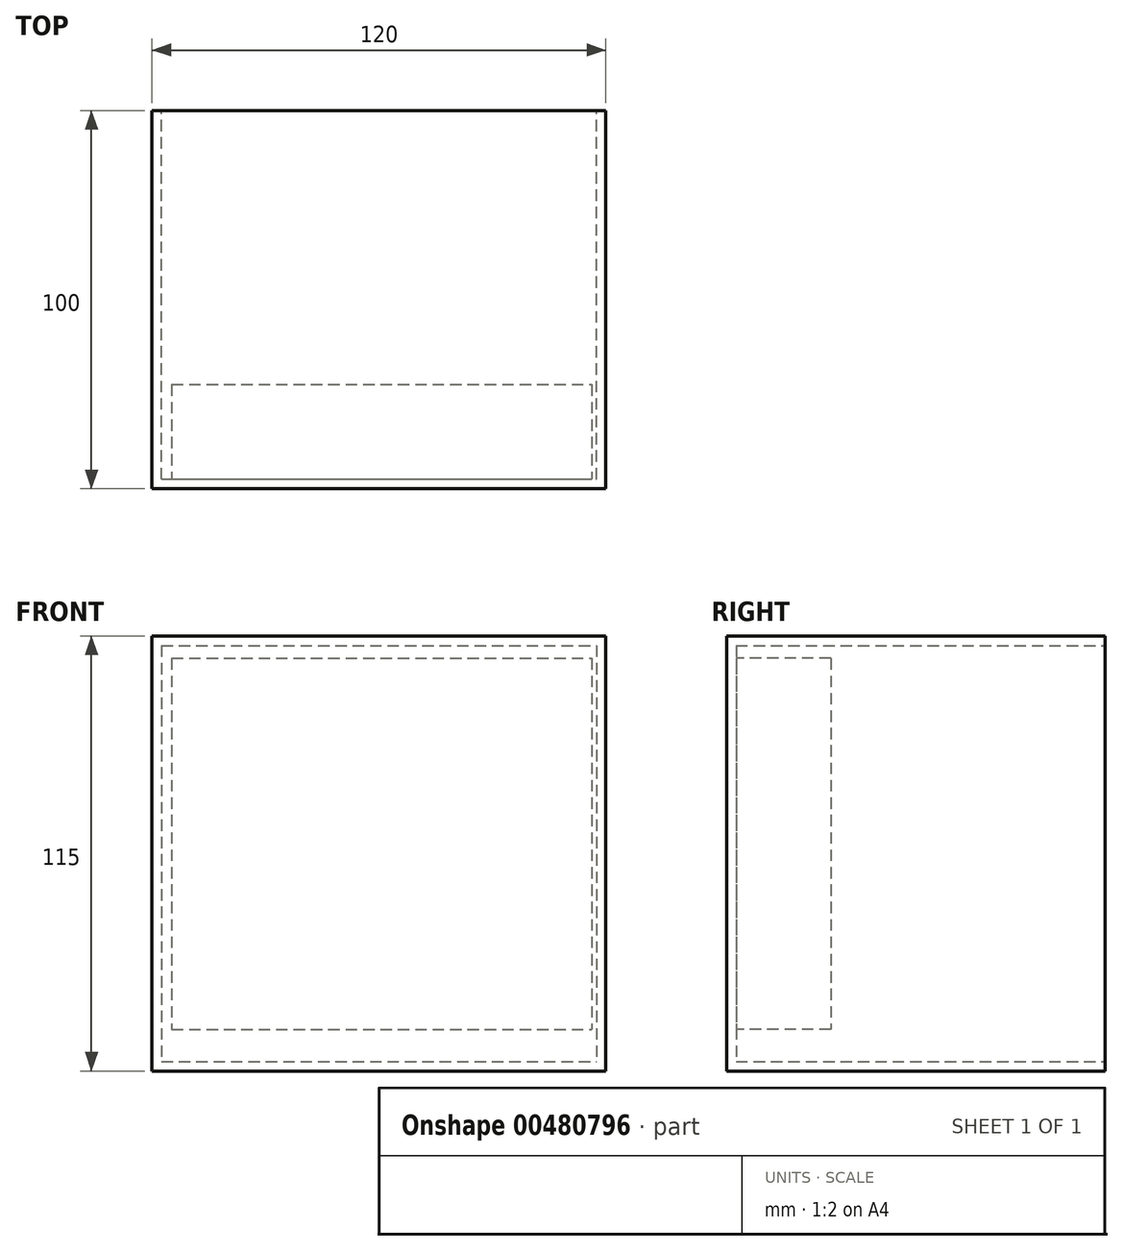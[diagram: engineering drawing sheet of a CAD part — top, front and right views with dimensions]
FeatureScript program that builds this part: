
annotation { "Feature Type Name" : "Feature", "Feature Type Description" : "" }
export const myFeature = defineFeature(function(context is Context, id is Id, definition is map)
    precondition{}
    {
        {
            var Q0;
            Q0=qCreatedBy(makeId("Front.planeOp"),FACE);
            var sketch = newSketch(context, id + "F0", { "sketchPlane" : qUnion([Q0])});
            skLineSegment(sketch, "E0.bottom", {"start": v(40, 25) * mm, "end": v(-40, 25) * mm});
            skLineSegment(sketch, "E0.top", {"start": v(40, -25) * mm, "end": v(-40, -25) * mm});
            skLineSegment(sketch, "E0.left", {"start": v(40, 25) * mm, "end": v(40, -25) * mm});
            skLineSegment(sketch, "E0.right", {"start": v(-40, 25) * mm, "end": v(-40, -25) * mm});
            skPoint(sketch, "E0.middle", {"position": v(0, 0) * mm});
            skLineSegment(sketch, "E1.bottom", {"start": v(-38.55, 20) * mm, "end": v(31.45, 20) * mm});
            skLineSegment(sketch, "E1.top", {"start": v(-38.55, -20) * mm, "end": v(31.45, -20) * mm});
            skLineSegment(sketch, "E1.left", {"start": v(-38.55, 20) * mm, "end": v(-38.55, -20) * mm});
            skLineSegment(sketch, "E1.right", {"start": v(31.45, 20) * mm, "end": v(31.45, -20) * mm});
            skPoint(sketch, "E1.middle", {"position": v(-3.55, 0) * mm});
            skSolve(sketch);
        }
        {
            var Q0;
            Q0=makeQuery(id+"F0.imprint","IMPRINT",FACE,{"disambiguationData":[TD([[makeQuery(id+"F0.imprint","IMPRINT",EDGE,{"derivedFrom":sQuery(id+"F0.wireOp",EDGE,"E1.bottom")}),-1.0]])]});
            extrude(context, id + "F1", {"entities" : qUnion([Q0]), "depth" : 25 * mm});
        }
        {
            var Q0;
            Q0=makeQuery(id+"F1.opExtrude","SWEPT_FACE",FACE,{"disambiguationData":[OSD([sQuery(id+"F0.wireOp",EDGE,"E1.left")])]});
            extrude(context, id + "F2", {"entities" : qUnion([Q0]), "operationType" : NewBodyOperationType.ADD, "depth" : 25 * mm});
        }
        {
            var Q0;
            Q0=makeQuery(id+"F2.opExtrude","CAP_FACE",FACE,{"disambiguationData":[OSD([sQuery(id+"F0.wireOp",EDGE,"E1.left")])],"isStart":false});
            extrude(context, id + "F3", {"entities" : qUnion([Q0]), "operationType" : NewBodyOperationType.ADD, "depth" : 25 * mm});
        }
        {
            var Q0;
            {var subQ0=sQuery(id+"F0.wireOp",EDGE,"E1.left");var subQ1=sQuery(id+"F0.wireOp",EDGE,"E1.bottom");Q0=makeQuery(id+"F3.boolean.opBoolean","MERGE",FACE,{"derivedFrom":[makeQuery(id+"F2.boolean.opBoolean","MERGE",FACE,{"derivedFrom":[makeQuery(id+"F1.opExtrude","SWEPT_FACE",FACE,{"disambiguationData":[OSD([subQ1])]}),makeQuery(id+"F2.opExtrude","SWEPT_FACE",FACE,{"disambiguationData":[OSD([subQ1,subQ0])]})]}),makeQuery(id+"F3.opExtrude","SWEPT_FACE",FACE,{"disambiguationData":[OSD([subQ1,subQ0])]})]});}
            extrude(context, id + "F4", {"entities" : qUnion([Q0]), "operationType" : NewBodyOperationType.ADD, "depth" : 25 * mm});
        }
        {
            var Q0;
            Q0=makeQuery(id+"F4.opExtrude","CAP_FACE",FACE,{"disambiguationData":[OSD([sQuery(id+"F0.wireOp",EDGE,"E1.bottom"),sQuery(id+"F0.wireOp",EDGE,"E1.left")])],"isStart":false});
            extrude(context, id + "F5", {"entities" : qUnion([Q0]), "operationType" : NewBodyOperationType.ADD, "depth" : 25 * mm});
        }
        {
            var Q0;
            {var subQ0=sQuery(id+"F0.wireOp",EDGE,"E1.left");var subQ1=sQuery(id+"F0.wireOp",EDGE,"E1.bottom");var subQ2=makeQuery(id+"F1.opExtrude","CAP_VERTEX",VERTEX,{"disambiguationData":[OSD([subQ1,subQ0])],"isStart":false});var subQ3=makeQuery(id+"F3.boolean.opBoolean","MERGE",EDGE,{"derivedFrom":[makeQuery(id+"F2.boolean.opBoolean","MERGE",EDGE,{"derivedFrom":[makeQuery(id+"F1.opExtrude","CAP_EDGE",EDGE,{"disambiguationData":[OSD([subQ1])],"isStart":false}),makeQuery(id+"F2.opExtrude","SWEPT_EDGE",EDGE,{"disambiguationData":[OSD([subQ1,subQ0]),TDD([subQ2])]})]}),makeQuery(id+"F3.opExtrude","SWEPT_EDGE",EDGE,{"disambiguationData":[OSD([subQ1,subQ0]),TDD([makeQuery(id+"F2.opExtrude","CAP_VERTEX",VERTEX,{"disambiguationData":[OSD([subQ1,subQ0]),TDD([subQ2])],"isStart":false})])]})]});var subQ4=makeQuery(id+"F1.opExtrude","CAP_EDGE",EDGE,{"disambiguationData":[OSD([subQ0])],"isStart":false});Q0=makeQuery(id+"F5.boolean.opBoolean","MERGE",FACE,{"derivedFrom":[makeQuery(id+"F4.boolean.opBoolean","MERGE",FACE,{"derivedFrom":[makeQuery(id+"F3.boolean.opBoolean","MERGE",FACE,{"derivedFrom":[makeQuery(id+"F2.boolean.opBoolean","MERGE",FACE,{"derivedFrom":[makeQuery(id+"F1.opExtrude","CAP_FACE",FACE,{"disambiguationData":[OSD([subQ1,sQuery(id+"F0.wireOp",EDGE,"E1.top"),subQ0,sQuery(id+"F0.wireOp",EDGE,"E1.right")])],"isStart":false}),makeQuery(id+"F2.opExtrude","SWEPT_FACE",FACE,{"disambiguationData":[OSD([subQ0]),TDD([subQ4])]})]}),makeQuery(id+"F3.opExtrude","SWEPT_FACE",FACE,{"disambiguationData":[OSD([subQ0]),TDD([makeQuery(id+"F2.opExtrude","CAP_EDGE",EDGE,{"disambiguationData":[OSD([subQ0]),TDD([subQ4])],"isStart":false})])]})]}),makeQuery(id+"F4.opExtrude","SWEPT_FACE",FACE,{"disambiguationData":[OSD([subQ1,subQ0]),TDD([subQ3])]})]}),makeQuery(id+"F5.opExtrude","SWEPT_FACE",FACE,{"disambiguationData":[OSD([subQ1,subQ0]),TDD([makeQuery(id+"F4.opExtrude","CAP_EDGE",EDGE,{"disambiguationData":[OSD([subQ1,subQ0]),TDD([subQ3])],"isStart":false})])]})]});}
            extrude(context, id + "F6", {"entities" : qUnion([Q0]), "operationType" : NewBodyOperationType.ADD, "depth" : 25 * mm});
        }
        {
            var Q0;
            Q0=makeQuery(id+"F6.opExtrude","CAP_FACE",FACE,{"disambiguationData":[OSD([sQuery(id+"F0.wireOp",EDGE,"E1.bottom"),sQuery(id+"F0.wireOp",EDGE,"E1.top"),sQuery(id+"F0.wireOp",EDGE,"E1.left"),sQuery(id+"F0.wireOp",EDGE,"E1.right")])],"isStart":false});
            extrude(context, id + "F7", {"entities" : qUnion([Q0]), "operationType" : NewBodyOperationType.ADD, "depth" : 25 * mm});
        }
        {
            var Q0;
            {var subQ0=sQuery(id+"F0.wireOp",EDGE,"E1.left");var subQ1=sQuery(id+"F0.wireOp",EDGE,"E1.bottom");var subQ2=makeQuery(id+"F1.opExtrude","CAP_VERTEX",VERTEX,{"disambiguationData":[OSD([subQ1,subQ0])],"isStart":true});var subQ3=makeQuery(id+"F3.boolean.opBoolean","MERGE",EDGE,{"derivedFrom":[makeQuery(id+"F2.boolean.opBoolean","MERGE",EDGE,{"derivedFrom":[makeQuery(id+"F1.opExtrude","CAP_EDGE",EDGE,{"disambiguationData":[OSD([subQ1])],"isStart":true}),makeQuery(id+"F2.opExtrude","SWEPT_EDGE",EDGE,{"disambiguationData":[OSD([subQ1,subQ0]),TDD([subQ2])]})]}),makeQuery(id+"F3.opExtrude","SWEPT_EDGE",EDGE,{"disambiguationData":[OSD([subQ1,subQ0]),TDD([makeQuery(id+"F2.opExtrude","CAP_VERTEX",VERTEX,{"disambiguationData":[OSD([subQ1,subQ0]),TDD([subQ2])],"isStart":false})])]})]});var subQ4=makeQuery(id+"F1.opExtrude","CAP_EDGE",EDGE,{"disambiguationData":[OSD([subQ0])],"isStart":true});Q0=makeQuery(id+"F5.boolean.opBoolean","MERGE",FACE,{"derivedFrom":[makeQuery(id+"F4.boolean.opBoolean","MERGE",FACE,{"derivedFrom":[makeQuery(id+"F3.boolean.opBoolean","MERGE",FACE,{"derivedFrom":[makeQuery(id+"F2.boolean.opBoolean","MERGE",FACE,{"derivedFrom":[makeQuery(id+"F1.opExtrude","CAP_FACE",FACE,{"disambiguationData":[OSD([subQ1,sQuery(id+"F0.wireOp",EDGE,"E1.top"),subQ0,sQuery(id+"F0.wireOp",EDGE,"E1.right")])],"isStart":true}),makeQuery(id+"F2.opExtrude","SWEPT_FACE",FACE,{"disambiguationData":[OSD([subQ0]),TDD([subQ4])]})]}),makeQuery(id+"F3.opExtrude","SWEPT_FACE",FACE,{"disambiguationData":[OSD([subQ0]),TDD([makeQuery(id+"F2.opExtrude","CAP_EDGE",EDGE,{"disambiguationData":[OSD([subQ0]),TDD([subQ4])],"isStart":false})])]})]}),makeQuery(id+"F4.opExtrude","SWEPT_FACE",FACE,{"disambiguationData":[OSD([subQ1,subQ0]),TDD([subQ3])]})]}),makeQuery(id+"F5.opExtrude","SWEPT_FACE",FACE,{"disambiguationData":[OSD([subQ1,subQ0]),TDD([makeQuery(id+"F4.opExtrude","CAP_EDGE",EDGE,{"disambiguationData":[OSD([subQ1,subQ0]),TDD([subQ3])],"isStart":false})])]})]});}
            extrude(context, id + "F8", {"entities" : qUnion([Q0]), "operationType" : NewBodyOperationType.ADD, "depth" : 25 * mm});
        }
        {
            var Q0;
            {var subQ0=sQuery(id+"F0.wireOp",EDGE,"E1.left");var subQ1=sQuery(id+"F0.wireOp",EDGE,"E1.bottom");var subQ2=makeQuery(id+"F1.opExtrude","CAP_VERTEX",VERTEX,{"disambiguationData":[OSD([subQ1,subQ0])],"isStart":true});var subQ3=makeQuery(id+"F1.opExtrude","CAP_VERTEX",VERTEX,{"disambiguationData":[OSD([subQ1,subQ0])],"isStart":false});var subQ4=makeQuery(id+"F5.opExtrude","CAP_EDGE",EDGE,{"disambiguationData":[OSD([subQ1,subQ0]),TDD([makeQuery(id+"F4.opExtrude","CAP_EDGE",EDGE,{"disambiguationData":[OSD([subQ1,subQ0]),TDD([makeQuery(id+"F3.boolean.opBoolean","MERGE",EDGE,{"derivedFrom":[makeQuery(id+"F2.boolean.opBoolean","MERGE",EDGE,{"derivedFrom":[makeQuery(id+"F1.opExtrude","CAP_EDGE",EDGE,{"disambiguationData":[OSD([subQ1])],"isStart":false}),makeQuery(id+"F2.opExtrude","SWEPT_EDGE",EDGE,{"disambiguationData":[OSD([subQ1,subQ0]),TDD([subQ3])]})]}),makeQuery(id+"F3.opExtrude","SWEPT_EDGE",EDGE,{"disambiguationData":[OSD([subQ1,subQ0]),TDD([makeQuery(id+"F2.opExtrude","CAP_VERTEX",VERTEX,{"disambiguationData":[OSD([subQ1,subQ0]),TDD([subQ3])],"isStart":false})])]})]})])],"isStart":false})])],"isStart":false});Q0=makeQuery(id+"F8.boolean.opBoolean","MERGE",FACE,{"derivedFrom":[makeQuery(id+"F7.boolean.opBoolean","MERGE",FACE,{"derivedFrom":[makeQuery(id+"F6.boolean.opBoolean","MERGE",FACE,{"derivedFrom":[makeQuery(id+"F5.opExtrude","CAP_FACE",FACE,{"disambiguationData":[OSD([subQ1,subQ0])],"isStart":false}),makeQuery(id+"F6.opExtrude","SWEPT_FACE",FACE,{"disambiguationData":[OSD([subQ1,subQ0]),TDD([subQ4])]})]}),makeQuery(id+"F7.opExtrude","SWEPT_FACE",FACE,{"disambiguationData":[OSD([subQ1,subQ0]),TDD([makeQuery(id+"F6.opExtrude","CAP_EDGE",EDGE,{"disambiguationData":[OSD([subQ1,subQ0]),TDD([subQ4])],"isStart":false})])]})]}),makeQuery(id+"F8.opExtrude","SWEPT_FACE",FACE,{"disambiguationData":[OSD([subQ1,subQ0]),TDD([makeQuery(id+"F5.opExtrude","CAP_EDGE",EDGE,{"disambiguationData":[OSD([subQ1,subQ0]),TDD([makeQuery(id+"F4.opExtrude","CAP_EDGE",EDGE,{"disambiguationData":[OSD([subQ1,subQ0]),TDD([makeQuery(id+"F3.boolean.opBoolean","MERGE",EDGE,{"derivedFrom":[makeQuery(id+"F2.boolean.opBoolean","MERGE",EDGE,{"derivedFrom":[makeQuery(id+"F1.opExtrude","CAP_EDGE",EDGE,{"disambiguationData":[OSD([subQ1])],"isStart":true}),makeQuery(id+"F2.opExtrude","SWEPT_EDGE",EDGE,{"disambiguationData":[OSD([subQ1,subQ0]),TDD([subQ2])]})]}),makeQuery(id+"F3.opExtrude","SWEPT_EDGE",EDGE,{"disambiguationData":[OSD([subQ1,subQ0]),TDD([makeQuery(id+"F2.opExtrude","CAP_VERTEX",VERTEX,{"disambiguationData":[OSD([subQ1,subQ0]),TDD([subQ2])],"isStart":false})])]})]})])],"isStart":false})])],"isStart":false})])]})]});}
            extrude(context, id + "F9", {"entities" : qUnion([Q0]), "operationType" : NewBodyOperationType.ADD, "depth" : 25 * mm});
        }
        {
            var Q0;
            {var subQ0=sQuery(id+"F0.wireOp",EDGE,"E1.left");var subQ1=sQuery(id+"F0.wireOp",EDGE,"E1.bottom");var subQ2=makeQuery(id+"F1.opExtrude","CAP_VERTEX",VERTEX,{"disambiguationData":[OSD([subQ1,subQ0])],"isStart":true});Q0=makeQuery(id+"F9.boolean.opBoolean","MERGE",FACE,{"derivedFrom":[makeQuery(id+"F8.opExtrude","CAP_FACE",FACE,{"disambiguationData":[OSD([subQ1,sQuery(id+"F0.wireOp",EDGE,"E1.top"),subQ0,sQuery(id+"F0.wireOp",EDGE,"E1.right")])],"isStart":false}),makeQuery(id+"F9.opExtrude","SWEPT_FACE",FACE,{"disambiguationData":[OSD([subQ1,subQ0]),TDD([makeQuery(id+"F8.opExtrude","CAP_EDGE",EDGE,{"disambiguationData":[OSD([subQ1,subQ0]),TDD([makeQuery(id+"F5.opExtrude","CAP_EDGE",EDGE,{"disambiguationData":[OSD([subQ1,subQ0]),TDD([makeQuery(id+"F4.opExtrude","CAP_EDGE",EDGE,{"disambiguationData":[OSD([subQ1,subQ0]),TDD([makeQuery(id+"F3.boolean.opBoolean","MERGE",EDGE,{"derivedFrom":[makeQuery(id+"F2.boolean.opBoolean","MERGE",EDGE,{"derivedFrom":[makeQuery(id+"F1.opExtrude","CAP_EDGE",EDGE,{"disambiguationData":[OSD([subQ1])],"isStart":true}),makeQuery(id+"F2.opExtrude","SWEPT_EDGE",EDGE,{"disambiguationData":[OSD([subQ1,subQ0]),TDD([subQ2])]})]}),makeQuery(id+"F3.opExtrude","SWEPT_EDGE",EDGE,{"disambiguationData":[OSD([subQ1,subQ0]),TDD([makeQuery(id+"F2.opExtrude","CAP_VERTEX",VERTEX,{"disambiguationData":[OSD([subQ1,subQ0]),TDD([subQ2])],"isStart":false})])]})]})])],"isStart":false})])],"isStart":false})])],"isStart":false})])]})]});}
            shell(context, id + "F10", {"entities" : qUnion([Q0]), "thickness" : 2.5 * mm});
        }
        {
            var Q0;
            Q0=makeQuery(id+"F10.opShell","OFFSET_FACE",FACE,{"disambiguationData":[OSD([sQuery(id+"F0.wireOp",EDGE,"E1.bottom"),sQuery(id+"F0.wireOp",EDGE,"E1.top"),sQuery(id+"F0.wireOp",EDGE,"E1.left"),sQuery(id+"F0.wireOp",EDGE,"E1.right")])]});
            var sketch = newSketch(context, id + "F11", { "sketchPlane" : qUnion([Q0])});
            skLineSegment(sketch, "E2.bottom", {"start": v(83.31, 89.13) * mm, "end": v(-27.73, 89.13) * mm});
            skLineSegment(sketch, "E2.top", {"start": v(83.31, -8.94) * mm, "end": v(-27.73, -8.94) * mm});
            skLineSegment(sketch, "E2.left", {"start": v(83.31, 89.13) * mm, "end": v(83.31, -8.94) * mm});
            skLineSegment(sketch, "E2.right", {"start": v(-27.73, 89.13) * mm, "end": v(-27.73, -8.94) * mm});
            skPoint(sketch, "E2.middle", {"position": v(27.79, 40.1) * mm});
            skSolve(sketch);
        }
        {
            var Q0;
            Q0=makeQuery(id+"F11.imprint","IMPRINT",FACE,{"disambiguationData":[TD([[makeQuery(id+"F11.imprint","IMPRINT",EDGE,{"derivedFrom":sQuery(id+"F11.wireOp",EDGE,"E2.bottom")}),1.0]])]});
            extrude(context, id + "F12", {"entities" : qUnion([Q0]), "operationType" : NewBodyOperationType.ADD, "depth" : 25 * mm});
        }
    });
